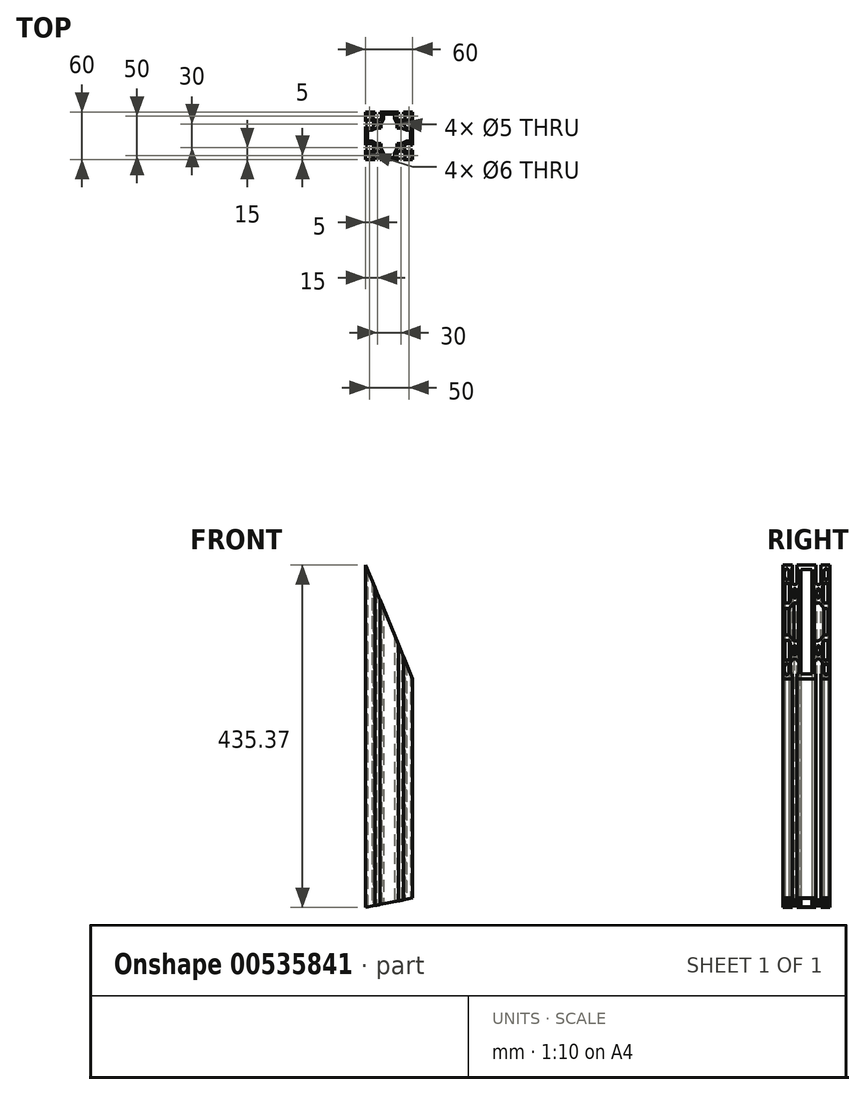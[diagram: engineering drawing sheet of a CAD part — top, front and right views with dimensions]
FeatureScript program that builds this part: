
annotation { "Feature Type Name" : "Feature", "Feature Type Description" : "" }
export const myFeature = defineFeature(function(context is Context, id is Id, definition is map)
    precondition{}
    {
        {
            var Q0;
            Q0=qCreatedBy(makeId("Top.planeOp"),FACE);
            var sketch = newSketch(context, id + "F0", { "sketchPlane" : qUnion([Q0])});
            skLineSegment(sketch, "E0.bottom", {"start": v(30, -30) * mm, "end": v(-30, -30) * mm});
            skLineSegment(sketch, "E0.top", {"start": v(30, 30) * mm, "end": v(-30, 30) * mm});
            skLineSegment(sketch, "E0.left", {"start": v(30, -30) * mm, "end": v(30, 30) * mm});
            skLineSegment(sketch, "E0.right", {"start": v(-30, -30) * mm, "end": v(-30, 30) * mm});
            skPoint(sketch, "E0.middle", {"position": v(0, 0) * mm});
            skLineSegment(sketch, "E1.top", {"start": v(-11.85, 30) * mm, "end": v(-18.15, 30) * mm});
            skLineSegment(sketch, "E1.left", {"start": v(-11.85, 27.5) * mm, "end": v(-11.85, 30) * mm});
            skLineSegment(sketch, "E1.right", {"start": v(-18.15, 27.5) * mm, "end": v(-18.15, 30) * mm});
            skPoint(sketch, "E1.middle", {"position": v(-15, 28.75) * mm});
            skLineSegment(sketch, "E2.bottom", {"start": v(-9.85, 27.5) * mm, "end": v(-11.85, 27.5) * mm});
            skLineSegment(sketch, "E2.left", {"start": v(-9.85, 27.5) * mm, "end": v(-9.85, 21.55) * mm});
            skLineSegment(sketch, "E2.right", {"start": v(-20.15, 27.5) * mm, "end": v(-20.15, 21.55) * mm});
            skPoint(sketch, "E2.middle", {"position": v(-15, 24.52) * mm});
            skArc(sketch, "E3", {"start": v(-20.15, 21.55) * mm, "mid": v(-15, 19.5) * mm, "end": v(-9.85, 21.55) * mm});
            skPoint(sketch, "E4.MirrorP", {"position": v(15, 24.52) * mm});
            skPoint(sketch, "E5.MirrorP", {"position": v(15, 28.75) * mm});
            skLineSegment(sketch, "E6.MirrorCS", {"start": v(11.85, 27.5) * mm, "end": v(11.85, 30) * mm});
            skLineSegment(sketch, "E7.MirrorCS", {"start": v(18.15, 27.5) * mm, "end": v(18.15, 30) * mm});
            skLineSegment(sketch, "E8.MirrorCS", {"start": v(9.85, 27.5) * mm, "end": v(11.85, 27.5) * mm});
            skLineSegment(sketch, "E9.MirrorCS", {"start": v(9.85, 27.5) * mm, "end": v(9.85, 21.55) * mm});
            skArc(sketch, "E10.MirrorCS", {"start": v(20.15, 21.55) * mm, "mid": v(15, 19.5) * mm, "end": v(9.85, 21.55) * mm});
            skLineSegment(sketch, "E11.MirrorCS", {"start": v(20.15, 27.5) * mm, "end": v(20.15, 21.55) * mm});
            skLineSegment(sketch, "E12.MirrorCS", {"start": v(11.85, 30) * mm, "end": v(18.15, 30) * mm});
            skLineSegment(sketch, "E13.1.0", {"start": v(27.5, 20.15) * mm, "end": v(21.55, 20.15) * mm});
            skLineSegment(sketch, "E13.1.1", {"start": v(27.5, 9.85) * mm, "end": v(21.55, 9.85) * mm});
            skArc(sketch, "E13.1.2", {"start": v(21.55, 20.15) * mm, "mid": v(19.5, 15) * mm, "end": v(21.55, 9.85) * mm});
            skLineSegment(sketch, "E13.1.3", {"start": v(27.5, -9.85) * mm, "end": v(21.55, -9.85) * mm});
            skLineSegment(sketch, "E13.1.4", {"start": v(27.5, -20.15) * mm, "end": v(21.55, -20.15) * mm});
            skPoint(sketch, "E13.1.5", {"position": v(28.75, 15) * mm});
            skPoint(sketch, "E13.1.6", {"position": v(28.75, -15) * mm});
            skArc(sketch, "E13.1.7", {"start": v(21.55, -20.15) * mm, "mid": v(19.5, -15) * mm, "end": v(21.55, -9.85) * mm});
            skPoint(sketch, "E13.1.8", {"position": v(24.52, -15) * mm});
            skPoint(sketch, "E13.1.9", {"position": v(24.52, 15) * mm});
            skLineSegment(sketch, "E13.1.10", {"start": v(27.5, 9.85) * mm, "end": v(27.5, 20.15) * mm});
            skLineSegment(sketch, "E13.1.11", {"start": v(27.5, -11.85) * mm, "end": v(27.5, -18.15) * mm});
            skLineSegment(sketch, "E13.1.12", {"start": v(30, 11.85) * mm, "end": v(30, 18.15) * mm});
            skLineSegment(sketch, "E13.1.13", {"start": v(30, -11.85) * mm, "end": v(30, -18.15) * mm});
            skLineSegment(sketch, "E13.1.14", {"start": v(27.5, 18.15) * mm, "end": v(30, 18.15) * mm});
            skLineSegment(sketch, "E13.1.15", {"start": v(27.5, 11.85) * mm, "end": v(30, 11.85) * mm});
            skLineSegment(sketch, "E13.1.16", {"start": v(27.5, 11.85) * mm, "end": v(27.5, 18.15) * mm});
            skLineSegment(sketch, "E13.1.17", {"start": v(27.5, -9.85) * mm, "end": v(27.5, -20.15) * mm});
            skLineSegment(sketch, "E13.1.18", {"start": v(27.5, -18.15) * mm, "end": v(30, -18.15) * mm});
            skLineSegment(sketch, "E13.1.19", {"start": v(27.5, -11.85) * mm, "end": v(30, -11.85) * mm});
            skLineSegment(sketch, "E13.2.0", {"start": v(20.15, -27.5) * mm, "end": v(20.15, -21.55) * mm});
            skLineSegment(sketch, "E13.2.1", {"start": v(9.85, -27.5) * mm, "end": v(9.85, -21.55) * mm});
            skArc(sketch, "E13.2.2", {"start": v(20.15, -21.55) * mm, "mid": v(15, -19.5) * mm, "end": v(9.85, -21.55) * mm});
            skLineSegment(sketch, "E13.2.3", {"start": v(-9.85, -27.5) * mm, "end": v(-9.85, -21.55) * mm});
            skLineSegment(sketch, "E13.2.4", {"start": v(-20.15, -27.5) * mm, "end": v(-20.15, -21.55) * mm});
            skPoint(sketch, "E13.2.5", {"position": v(15, -28.75) * mm});
            skPoint(sketch, "E13.2.6", {"position": v(-15, -28.75) * mm});
            skArc(sketch, "E13.2.7", {"start": v(-20.15, -21.55) * mm, "mid": v(-15, -19.5) * mm, "end": v(-9.85, -21.55) * mm});
            skPoint(sketch, "E13.2.8", {"position": v(-15, -24.52) * mm});
            skPoint(sketch, "E13.2.9", {"position": v(15, -24.52) * mm});
            skLineSegment(sketch, "E13.2.10", {"start": v(9.85, -27.5) * mm, "end": v(20.15, -27.5) * mm});
            skLineSegment(sketch, "E13.2.11", {"start": v(-11.85, -27.5) * mm, "end": v(-18.15, -27.5) * mm});
            skLineSegment(sketch, "E13.2.12", {"start": v(11.85, -30) * mm, "end": v(18.15, -30) * mm});
            skLineSegment(sketch, "E13.2.13", {"start": v(-11.85, -30) * mm, "end": v(-18.15, -30) * mm});
            skLineSegment(sketch, "E13.2.14", {"start": v(18.15, -27.5) * mm, "end": v(18.15, -30) * mm});
            skLineSegment(sketch, "E13.2.15", {"start": v(11.85, -27.5) * mm, "end": v(11.85, -30) * mm});
            skLineSegment(sketch, "E13.2.16", {"start": v(11.85, -27.5) * mm, "end": v(18.15, -27.5) * mm});
            skLineSegment(sketch, "E13.2.17", {"start": v(-9.85, -27.5) * mm, "end": v(-20.15, -27.5) * mm});
            skLineSegment(sketch, "E13.2.18", {"start": v(-18.15, -27.5) * mm, "end": v(-18.15, -30) * mm});
            skLineSegment(sketch, "E13.2.19", {"start": v(-11.85, -27.5) * mm, "end": v(-11.85, -30) * mm});
            skLineSegment(sketch, "E13.3.0", {"start": v(-27.5, -20.15) * mm, "end": v(-21.55, -20.15) * mm});
            skLineSegment(sketch, "E13.3.1", {"start": v(-27.5, -9.85) * mm, "end": v(-21.55, -9.85) * mm});
            skArc(sketch, "E13.3.2", {"start": v(-21.55, -20.15) * mm, "mid": v(-19.5, -15) * mm, "end": v(-21.55, -9.85) * mm});
            skLineSegment(sketch, "E13.3.3", {"start": v(-27.5, 9.85) * mm, "end": v(-21.55, 9.85) * mm});
            skLineSegment(sketch, "E13.3.4", {"start": v(-27.5, 20.15) * mm, "end": v(-21.55, 20.15) * mm});
            skPoint(sketch, "E13.3.5", {"position": v(-28.75, -15) * mm});
            skPoint(sketch, "E13.3.6", {"position": v(-28.75, 15) * mm});
            skArc(sketch, "E13.3.7", {"start": v(-21.55, 20.15) * mm, "mid": v(-19.5, 15) * mm, "end": v(-21.55, 9.85) * mm});
            skPoint(sketch, "E13.3.8", {"position": v(-24.52, 15) * mm});
            skPoint(sketch, "E13.3.9", {"position": v(-24.52, -15) * mm});
            skLineSegment(sketch, "E13.3.10", {"start": v(-27.5, -9.85) * mm, "end": v(-27.5, -20.15) * mm});
            skLineSegment(sketch, "E13.3.11", {"start": v(-27.5, 11.85) * mm, "end": v(-27.5, 18.15) * mm});
            skLineSegment(sketch, "E13.3.12", {"start": v(-30, -11.85) * mm, "end": v(-30, -18.15) * mm});
            skLineSegment(sketch, "E13.3.13", {"start": v(-30, 11.85) * mm, "end": v(-30, 18.15) * mm});
            skLineSegment(sketch, "E13.3.14", {"start": v(-27.5, -18.15) * mm, "end": v(-30, -18.15) * mm});
            skLineSegment(sketch, "E13.3.15", {"start": v(-27.5, -11.85) * mm, "end": v(-30, -11.85) * mm});
            skLineSegment(sketch, "E13.3.16", {"start": v(-27.5, -11.85) * mm, "end": v(-27.5, -18.15) * mm});
            skLineSegment(sketch, "E13.3.17", {"start": v(-27.5, 9.85) * mm, "end": v(-27.5, 20.15) * mm});
            skLineSegment(sketch, "E13.3.18", {"start": v(-27.5, 18.15) * mm, "end": v(-30, 18.15) * mm});
            skLineSegment(sketch, "E13.3.19", {"start": v(-27.5, 11.85) * mm, "end": v(-30, 11.85) * mm});
            skLineSegment(sketch, "E13.anchor1", {"start": v(0, 0) * mm, "end": v(-20.15, 21.55) * mm, "construction": true});
            skLineSegment(sketch, "E13.anchor2", {"start": v(0, 0) * mm, "end": v(-21.55, -20.15) * mm, "construction": true});
            skLineSegment(sketch, "E14.trimOffspring", {"start": v(-18.15, 27.5) * mm, "end": v(-20.15, 27.5) * mm});
            skLineSegment(sketch, "E15.trimOffspring", {"start": v(18.15, 27.5) * mm, "end": v(20.15, 27.5) * mm});
            skCircle(sketch, "E16", {"center": v(-15, 15) * mm, "radius": 2.5 * mm});
            skCircle(sketch, "E17", {"center": v(-25, 25) * mm, "radius": 3 * mm});
            skCircle(sketch, "E18.MirrorC", {"center": v(25, 25) * mm, "radius": 3 * mm});
            skCircle(sketch, "E19.MirrorC", {"center": v(25, -25) * mm, "radius": 3 * mm});
            skCircle(sketch, "E20.MirrorC", {"center": v(-25, -25) * mm, "radius": 3 * mm});
            skCircle(sketch, "E21.MirrorC", {"center": v(15, 15) * mm, "radius": 2.5 * mm});
            skCircle(sketch, "E22.MirrorC", {"center": v(15, -15) * mm, "radius": 2.5 * mm});
            skCircle(sketch, "E23.MirrorC", {"center": v(-15, -15) * mm, "radius": 2.5 * mm});
            skLineSegment(sketch, "E24", {"start": v(-7, 27.5) * mm, "end": v(0, 27.5) * mm});
            skLineSegment(sketch, "E25", {"start": v(-7, 27.5) * mm, "end": v(-7, 22) * mm});
            skLineSegment(sketch, "E26", {"start": v(-10, 10) * mm, "end": v(-10, 16) * mm});
            skLineSegment(sketch, "E27", {"start": v(-10, 16) * mm, "end": v(-7, 22) * mm});
            skLineSegment(sketch, "E28.MirrorCS", {"start": v(10, 10) * mm, "end": v(10, 16) * mm});
            skLineSegment(sketch, "E29.MirrorCS", {"start": v(10, 16) * mm, "end": v(7, 22) * mm});
            skLineSegment(sketch, "E30.MirrorCS", {"start": v(7, 27.5) * mm, "end": v(0, 27.5) * mm});
            skLineSegment(sketch, "E31.MirrorCS", {"start": v(7, 27.5) * mm, "end": v(7, 22) * mm});
            skLineSegment(sketch, "E32.1.0", {"start": v(-10, -10) * mm, "end": v(-16, -10) * mm});
            skLineSegment(sketch, "E32.1.1", {"start": v(-16, -10) * mm, "end": v(-22, -7) * mm});
            skLineSegment(sketch, "E32.1.2", {"start": v(-27.5, -7) * mm, "end": v(-22, -7) * mm});
            skLineSegment(sketch, "E32.1.3", {"start": v(-27.5, -7) * mm, "end": v(-27.5, 0) * mm});
            skLineSegment(sketch, "E32.1.4", {"start": v(-27.5, 7) * mm, "end": v(-27.5, 0) * mm});
            skLineSegment(sketch, "E32.1.5", {"start": v(-27.5, 7) * mm, "end": v(-22, 7) * mm});
            skLineSegment(sketch, "E32.1.6", {"start": v(-16, 10) * mm, "end": v(-22, 7) * mm});
            skLineSegment(sketch, "E32.1.7", {"start": v(-10, 10) * mm, "end": v(-16, 10) * mm});
            skLineSegment(sketch, "E32.2.0", {"start": v(10, -10) * mm, "end": v(10, -16) * mm});
            skLineSegment(sketch, "E32.2.1", {"start": v(10, -16) * mm, "end": v(7, -22) * mm});
            skLineSegment(sketch, "E32.2.2", {"start": v(7, -27.5) * mm, "end": v(7, -22) * mm});
            skLineSegment(sketch, "E32.2.3", {"start": v(7, -27.5) * mm, "end": v(0, -27.5) * mm});
            skLineSegment(sketch, "E32.2.4", {"start": v(-7, -27.5) * mm, "end": v(0, -27.5) * mm});
            skLineSegment(sketch, "E32.2.5", {"start": v(-7, -27.5) * mm, "end": v(-7, -22) * mm});
            skLineSegment(sketch, "E32.2.6", {"start": v(-10, -16) * mm, "end": v(-7, -22) * mm});
            skLineSegment(sketch, "E32.2.7", {"start": v(-10, -10) * mm, "end": v(-10, -16) * mm});
            skLineSegment(sketch, "E32.3.0", {"start": v(10, 10) * mm, "end": v(16, 10) * mm});
            skLineSegment(sketch, "E32.3.1", {"start": v(16, 10) * mm, "end": v(22, 7) * mm});
            skLineSegment(sketch, "E32.3.2", {"start": v(27.5, 7) * mm, "end": v(22, 7) * mm});
            skLineSegment(sketch, "E32.3.3", {"start": v(27.5, 7) * mm, "end": v(27.5, 0) * mm});
            skLineSegment(sketch, "E32.3.4", {"start": v(27.5, -7) * mm, "end": v(27.5, 0) * mm});
            skLineSegment(sketch, "E32.3.5", {"start": v(27.5, -7) * mm, "end": v(22, -7) * mm});
            skLineSegment(sketch, "E32.3.6", {"start": v(16, -10) * mm, "end": v(22, -7) * mm});
            skLineSegment(sketch, "E32.3.7", {"start": v(10, -10) * mm, "end": v(16, -10) * mm});
            skSolve(sketch);
        }
        {
            var Q0;
            {var subQ30=sQuery(id+"F0.wireOp",EDGE,"E1.left");Q0=makeQuery(id+"F0.imprint","IMPRINT",FACE,{"disambiguationData":[TD([[makeQuery(id+"F0.imprint","IMPRINT",EDGE,{"derivedFrom":subQ30}),-1.0]])]});}
            extrude(context, id + "F1", {"entities" : qUnion([Q0]), "depth" : 435.37 * mm, "offsetDistance" : 25 * mm});
        }
        {
            var Q0;
            Q0=makeQuery(id+"F1.opExtrude","SWEPT_EDGE",EDGE,{"disambiguationData":[OSD([sQuery(id+"F0.wireOp",EDGE,"E24"),sQuery(id+"F0.wireOp",EDGE,"E25")])]});
            var Q1;
            Q1=makeQuery(id+"F1.opExtrude","SWEPT_EDGE",EDGE,{"disambiguationData":[OSD([sQuery(id+"F0.wireOp",EDGE,"E30.MirrorCS"),sQuery(id+"F0.wireOp",EDGE,"E31.MirrorCS")])]});
            var Q2;
            Q2=makeQuery(id+"F1.opExtrude","SWEPT_EDGE",EDGE,{"disambiguationData":[OSD([sQuery(id+"F0.wireOp",EDGE,"840db5bc-c403-45cd-90c7-254e62d9e8c5.3.2"),sQuery(id+"F0.wireOp",EDGE,"840db5bc-c403-45cd-90c7-254e62d9e8c5.3.3")])]});
            var Q3;
            Q3=makeQuery(id+"F1.opExtrude","SWEPT_EDGE",EDGE,{"disambiguationData":[OSD([sQuery(id+"F0.wireOp",EDGE,"840db5bc-c403-45cd-90c7-254e62d9e8c5.3.4"),sQuery(id+"F0.wireOp",EDGE,"840db5bc-c403-45cd-90c7-254e62d9e8c5.3.5")])]});
            var Q4;
            Q4=makeQuery(id+"F1.opExtrude","SWEPT_EDGE",EDGE,{"disambiguationData":[OSD([sQuery(id+"F0.wireOp",EDGE,"840db5bc-c403-45cd-90c7-254e62d9e8c5.1.4"),sQuery(id+"F0.wireOp",EDGE,"840db5bc-c403-45cd-90c7-254e62d9e8c5.1.5")])]});
            var Q5;
            Q5=makeQuery(id+"F1.opExtrude","SWEPT_EDGE",EDGE,{"disambiguationData":[OSD([sQuery(id+"F0.wireOp",EDGE,"840db5bc-c403-45cd-90c7-254e62d9e8c5.1.2"),sQuery(id+"F0.wireOp",EDGE,"840db5bc-c403-45cd-90c7-254e62d9e8c5.1.3")])]});
            var Q6;
            Q6=makeQuery(id+"F1.opExtrude","SWEPT_EDGE",EDGE,{"disambiguationData":[OSD([sQuery(id+"F0.wireOp",EDGE,"840db5bc-c403-45cd-90c7-254e62d9e8c5.2.2"),sQuery(id+"F0.wireOp",EDGE,"840db5bc-c403-45cd-90c7-254e62d9e8c5.2.3")])]});
            var Q7;
            Q7=makeQuery(id+"F1.opExtrude","SWEPT_EDGE",EDGE,{"disambiguationData":[OSD([sQuery(id+"F0.wireOp",EDGE,"840db5bc-c403-45cd-90c7-254e62d9e8c5.2.4"),sQuery(id+"F0.wireOp",EDGE,"840db5bc-c403-45cd-90c7-254e62d9e8c5.2.5")])]});
            fillet(context, id + "F2", {"entities" : qUnion([Q0, Q1, Q2, Q3, Q4, Q5, Q6, Q7]), "radius" : 2 * mm, "tangentPropagation" : true, "allowEdgeOverflow" : false});
        }
        {
            var Q0;
            Q0=makeQuery(id+"F1.opExtrude","SWEPT_EDGE",EDGE,{"disambiguationData":[OSD([sQuery(id+"F0.wireOp",EDGE,"E26"),sQuery(id+"F0.wireOp",EDGE,"E27")])]});
            var Q1;
            Q1=makeQuery(id+"F1.opExtrude","SWEPT_EDGE",EDGE,{"disambiguationData":[OSD([sQuery(id+"F0.wireOp",EDGE,"E28.MirrorCS"),sQuery(id+"F0.wireOp",EDGE,"E29.MirrorCS")])]});
            var Q2;
            Q2=makeQuery(id+"F1.opExtrude","SWEPT_EDGE",EDGE,{"disambiguationData":[OSD([sQuery(id+"F0.wireOp",EDGE,"840db5bc-c403-45cd-90c7-254e62d9e8c5.3.0"),sQuery(id+"F0.wireOp",EDGE,"840db5bc-c403-45cd-90c7-254e62d9e8c5.3.1")])]});
            var Q3;
            Q3=makeQuery(id+"F1.opExtrude","SWEPT_EDGE",EDGE,{"disambiguationData":[OSD([sQuery(id+"F0.wireOp",EDGE,"840db5bc-c403-45cd-90c7-254e62d9e8c5.1.6"),sQuery(id+"F0.wireOp",EDGE,"840db5bc-c403-45cd-90c7-254e62d9e8c5.1.7")])]});
            var Q4;
            Q4=makeQuery(id+"F1.opExtrude","SWEPT_EDGE",EDGE,{"disambiguationData":[OSD([sQuery(id+"F0.wireOp",EDGE,"840db5bc-c403-45cd-90c7-254e62d9e8c5.1.0"),sQuery(id+"F0.wireOp",EDGE,"840db5bc-c403-45cd-90c7-254e62d9e8c5.1.1")])]});
            var Q5;
            Q5=makeQuery(id+"F1.opExtrude","SWEPT_EDGE",EDGE,{"disambiguationData":[OSD([sQuery(id+"F0.wireOp",EDGE,"840db5bc-c403-45cd-90c7-254e62d9e8c5.3.6"),sQuery(id+"F0.wireOp",EDGE,"840db5bc-c403-45cd-90c7-254e62d9e8c5.3.7")])]});
            var Q6;
            Q6=makeQuery(id+"F1.opExtrude","SWEPT_EDGE",EDGE,{"disambiguationData":[OSD([sQuery(id+"F0.wireOp",EDGE,"840db5bc-c403-45cd-90c7-254e62d9e8c5.2.0"),sQuery(id+"F0.wireOp",EDGE,"840db5bc-c403-45cd-90c7-254e62d9e8c5.2.1")])]});
            var Q7;
            Q7=makeQuery(id+"F1.opExtrude","SWEPT_EDGE",EDGE,{"disambiguationData":[OSD([sQuery(id+"F0.wireOp",EDGE,"840db5bc-c403-45cd-90c7-254e62d9e8c5.2.6"),sQuery(id+"F0.wireOp",EDGE,"840db5bc-c403-45cd-90c7-254e62d9e8c5.2.7")])]});
            fillet(context, id + "F3", {"entities" : qUnion([Q0, Q1, Q2, Q3, Q4, Q5, Q6, Q7]), "radius" : 7 * mm, "tangentPropagation" : true, "allowEdgeOverflow" : false});
        }
        {
            var Q0;
            Q0=qCreatedBy(makeId("Front.planeOp"),FACE);
            var sketch = newSketch(context, id + "F4", { "sketchPlane" : qUnion([Q0])});
            skLineSegment(sketch, "E33.bottom", {"start": v(176.13, -193.02) * mm, "end": v(131.35, 32.1) * mm});
            skLineSegment(sketch, "E33.top", {"start": v(14.78, -225.12) * mm, "end": v(-30, 0) * mm});
            skLineSegment(sketch, "E33.left", {"start": v(176.13, -193.02) * mm, "end": v(14.78, -225.12) * mm});
            skLineSegment(sketch, "E33.right", {"start": v(131.35, 32.1) * mm, "end": v(-30, 0) * mm});
            skLineSegment(sketch, "E34.bottom", {"start": v(-30, 435.37) * mm, "end": v(207.06, 533.56) * mm});
            skLineSegment(sketch, "E34.top", {"start": v(64.67, 206.82) * mm, "end": v(301.73, 305.01) * mm});
            skLineSegment(sketch, "E34.left", {"start": v(-30, 435.37) * mm, "end": v(64.67, 206.82) * mm});
            skLineSegment(sketch, "E34.right", {"start": v(207.06, 533.56) * mm, "end": v(301.73, 305.01) * mm});
            skSolve(sketch);
        }
        {
            var Q0;
            Q0 = qSketchRegion(id + "F4", true);
            extrude(context, id + "F5", {"entities" : qUnion([Q0]), "operationType" : NewBodyOperationType.REMOVE, "depth" : 30 * mm, "offsetDistance" : 25 * mm, "hasSecondDirection" : true, "secondDirectionOppositeDirection" : true, "secondDirectionDepth" : 30 * mm});
        }
    });
